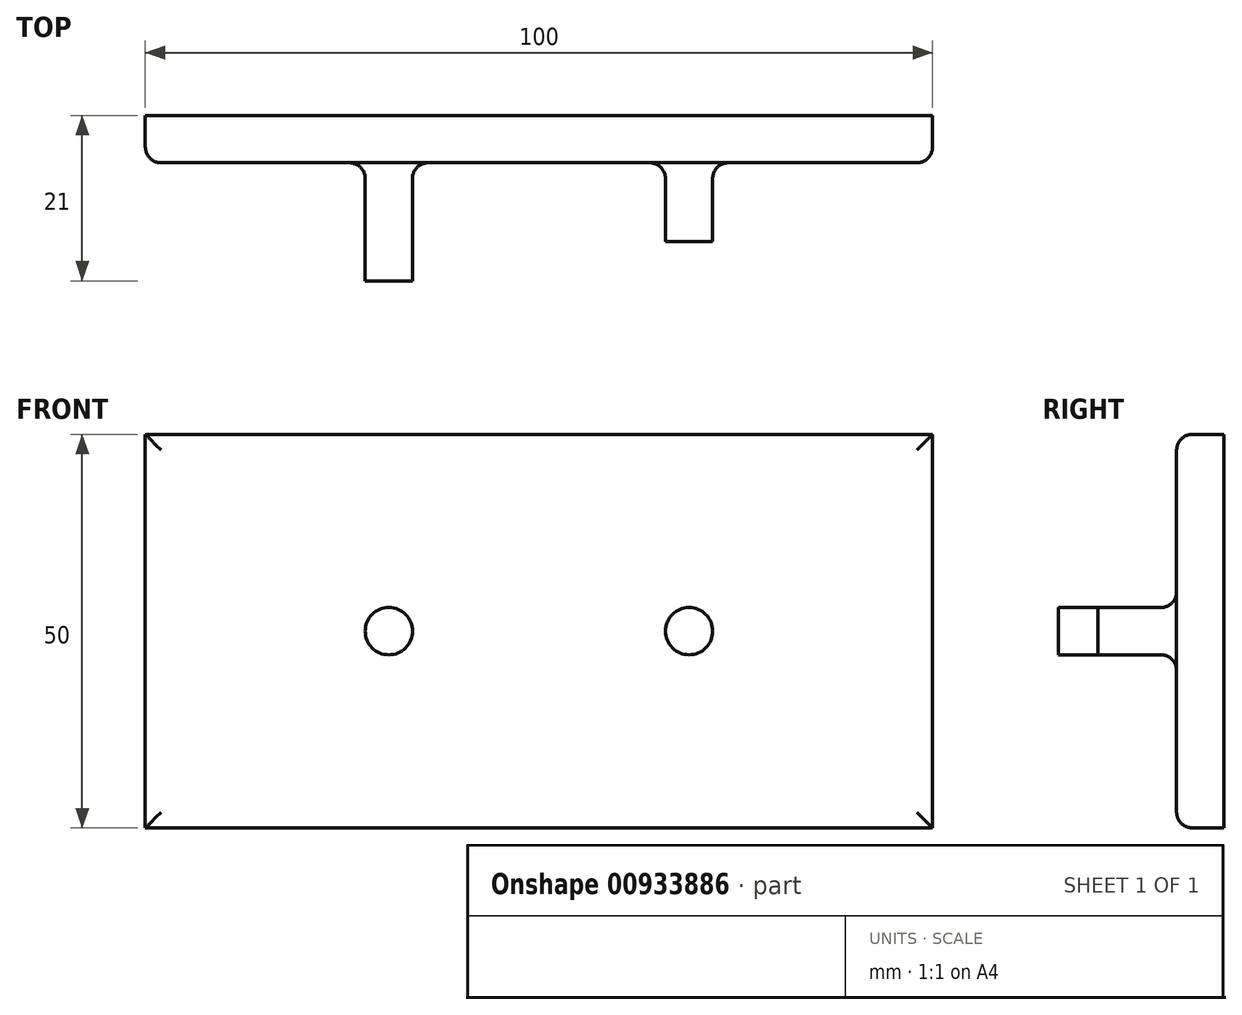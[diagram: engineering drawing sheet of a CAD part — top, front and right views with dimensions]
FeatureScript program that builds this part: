
annotation { "Feature Type Name" : "Feature", "Feature Type Description" : "" }
export const myFeature = defineFeature(function(context is Context, id is Id, definition is map)
    precondition{}
    {
        {
            var Q0;
            Q0=qCreatedBy(makeId("Front.planeOp"),FACE);
            var sketch = newSketch(context, id + "F0", { "sketchPlane" : qUnion([Q0])});
            skLineSegment(sketch, "E0.bottom", {"start": v(50, 25) * mm, "end": v(-50, 25) * mm});
            skLineSegment(sketch, "E0.top", {"start": v(50, -25) * mm, "end": v(-50, -25) * mm});
            skLineSegment(sketch, "E0.left", {"start": v(50, 25) * mm, "end": v(50, -25) * mm});
            skLineSegment(sketch, "E0.right", {"start": v(-50, 25) * mm, "end": v(-50, -25) * mm});
            skPoint(sketch, "E0.middle", {"position": v(0, 0) * mm});
            skSolve(sketch);
        }
        {
            var Q0;
            Q0 = qSketchRegion(id + "F0", true);
            extrude(context, id + "F1", {"entities" : qUnion([Q0]), "depth" : 6 * mm, "offsetDistance" : 25 * mm});
        }
        {
            var Q0;
            Q0=makeQuery(id+"F1.opExtrude","CAP_FACE",FACE,{"disambiguationData":[OSD([sQuery(id+"F0.wireOp",EDGE,"E0.bottom"),sQuery(id+"F0.wireOp",EDGE,"E0.top"),sQuery(id+"F0.wireOp",EDGE,"E0.left"),sQuery(id+"F0.wireOp",EDGE,"E0.right")])],"isStart":false});
            var sketch = newSketch(context, id + "F2", { "sketchPlane" : qUnion([Q0])});
            skCircle(sketch, "E1", {"center": v(-19.07, 0) * mm, "radius": 3 * mm});
            skCircle(sketch, "E2", {"center": v(19.07, 0) * mm, "radius": 3 * mm});
            skSolve(sketch);
        }
        {
            var Q0;
            Q0 = qSketchRegion(id + "F2", true);
            extrude(context, id + "F3", {"entities" : qUnion([Q0]), "operationType" : NewBodyOperationType.ADD, "depth" : 10 * mm, "offsetDistance" : 25 * mm});
        }
        {
            var Q0;
            Q0=makeQuery(id+"F1.opExtrude","CAP_FACE",FACE,{"disambiguationData":[OSD([sQuery(id+"F0.wireOp",EDGE,"E0.bottom"),sQuery(id+"F0.wireOp",EDGE,"E0.top"),sQuery(id+"F0.wireOp",EDGE,"E0.left"),sQuery(id+"F0.wireOp",EDGE,"E0.right")])],"isStart":false});
            fillet(context, id + "F4", {"entities" : qUnion([Q0]), "radius" : 2 * mm, "tangentPropagation" : true, "allowEdgeOverflow" : false});
        }
        {
            var Q0;
            Q0=makeQuery(id+"F3.opExtrude","CAP_FACE",FACE,{"disambiguationData":[OSD([sQuery(id+"F2.wireOp",EDGE,"E1")])],"isStart":false});
            var sketch = newSketch(context, id + "F5", { "sketchPlane" : qUnion([Q0])});
            skCircle(sketch, "E3", {"center": v(-19.07, 0) * mm, "radius": 3 * mm});
            skSolve(sketch);
        }
        {
            var Q0;
            Q0 = qSketchRegion(id + "F5", true);
            extrude(context, id + "F6", {"entities" : qUnion([Q0]), "operationType" : NewBodyOperationType.ADD, "depth" : 5 * mm, "offsetDistance" : 25 * mm});
        }
    });
